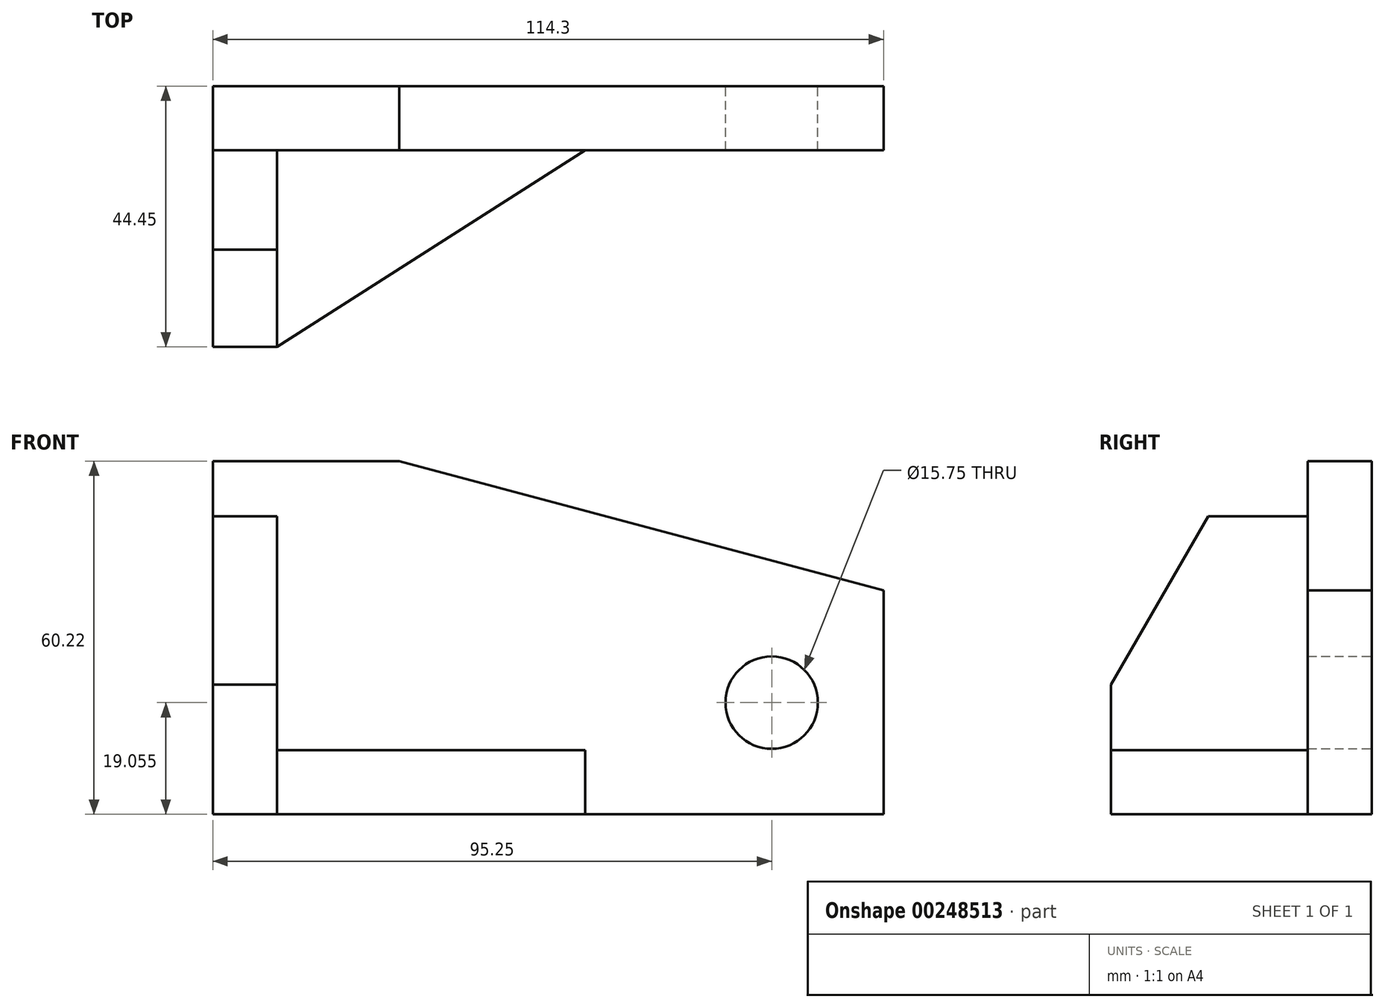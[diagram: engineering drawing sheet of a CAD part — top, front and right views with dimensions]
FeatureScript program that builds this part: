
annotation { "Feature Type Name" : "Feature", "Feature Type Description" : "" }
export const myFeature = defineFeature(function(context is Context, id is Id, definition is map)
    precondition{}
    {
        {
            var Q0;
            Q0=qCreatedBy(makeId("Front.planeOp"),FACE);
            var sketch = newSketch(context, id + "F0", { "sketchPlane" : qUnion([Q0])});
            skLineSegment(sketch, "E0.bottom", {"start": v(-63.5, 14.02) * mm, "end": v(-31.74, 14.04) * mm});
            skLineSegment(sketch, "E0.left", {"start": v(-63.5, 14.02) * mm, "end": v(-63.5, -46.18) * mm});
            skLineSegment(sketch, "E1", {"start": v(-31.74, 14.04) * mm, "end": v(50.8, -8.02) * mm});
            skLineSegment(sketch, "E2.left", {"start": v(50.8, -8.02) * mm, "end": v(50.8, -46.18) * mm});
            skLineSegment(sketch, "E3", {"start": v(-63.5, -46.18) * mm, "end": v(50.8, -46.18) * mm});
            skCircle(sketch, "E4", {"center": v(31.75, -27.13) * mm, "radius": 7.87 * mm});
            skPoint(sketch, "E5", {"position": v(0, -46.18) * mm});
            skSolve(sketch);
        }
        {
            var Q0;
            Q0 = qSketchRegion(id + "F0", true);
            extrude(context, id + "F1", {"entities" : qUnion([Q0]), "depth" : 10.92 * mm});
        }
        {
            var Q0;
            Q0=qCreatedBy(makeId("Right.planeOp"),FACE);
            var sketch = newSketch(context, id + "F2", { "sketchPlane" : qUnion([Q0])});
            skLineSegment(sketch, "E6", {"start": v(-44.45, -24.06) * mm, "end": v(-44.45, -46.16) * mm});
            skLineSegment(sketch, "E7", {"start": v(-10.92, -46.18) * mm, "end": v(-10.92, 4.62) * mm});
            skLineSegment(sketch, "E8", {"start": v(-10.92, 4.62) * mm, "end": v(-27.89, 4.62) * mm});
            skLineSegment(sketch, "E9", {"start": v(-27.89, 4.62) * mm, "end": v(-44.45, -24.06) * mm});
            skLineSegment(sketch, "E10", {"start": v(-44.45, -46.16) * mm, "end": v(-10.92, -46.18) * mm});
            skSolve(sketch);
        }
        {
            var Q0;
            Q0 = qSketchRegion(id + "F2", true);
            var Q1;
            Q1=makeQuery(id+"F1.opExtrude","SWEPT_FACE",FACE,{"disambiguationData":[OSD([sQuery(id+"F0.wireOp",EDGE,"E0.left")])]});
            extrude(context, id + "F3", {"entities" : qUnion([Q0]), "operationType" : NewBodyOperationType.ADD, "endBound" : BoundingType.UP_TO_SURFACE, "oppositeDirection" : true, "endBoundEntityFace" : qUnion([Q1]), "depth" : 54.6 * mm, "hasSecondDirection" : true, "secondDirectionOppositeDirection" : true, "secondDirectionDepth" : 52.58 * mm});
        }
        {
            var Q0;
            Q0=makeQuery(id+"F1.opExtrude","SWEPT_FACE",FACE,{"disambiguationData":[OSD([sQuery(id+"F0.wireOp",EDGE,"E3")])]});
            var sketch = newSketch(context, id + "F4", { "sketchPlane" : qUnion([Q0])});
            skLineSegment(sketch, "E11", {"start": v(-52.58, 44.45) * mm, "end": v(0, 10.92) * mm});
            skLineSegment(sketch, "E12", {"start": v(-52.58, 44.45) * mm, "end": v(-52.58, 10.92) * mm});
            skSolve(sketch);
        }
        {
            var Q0;
            {var subQ0=sQuery(id+"F4.wireOp",EDGE,"E11");Q0=makeQuery(id+"F4.imprint","IMPRINT",FACE,{"disambiguationData":[TD([[makeQuery(id+"F4.imprint","IMPRINT",EDGE,{"derivedFrom":subQ0}),-1.0]])]});}
            extrude(context, id + "F5", {"entities" : qUnion([Q0]), "operationType" : NewBodyOperationType.ADD, "oppositeDirection" : true, "depth" : 10.92 * mm});
        }
    });
